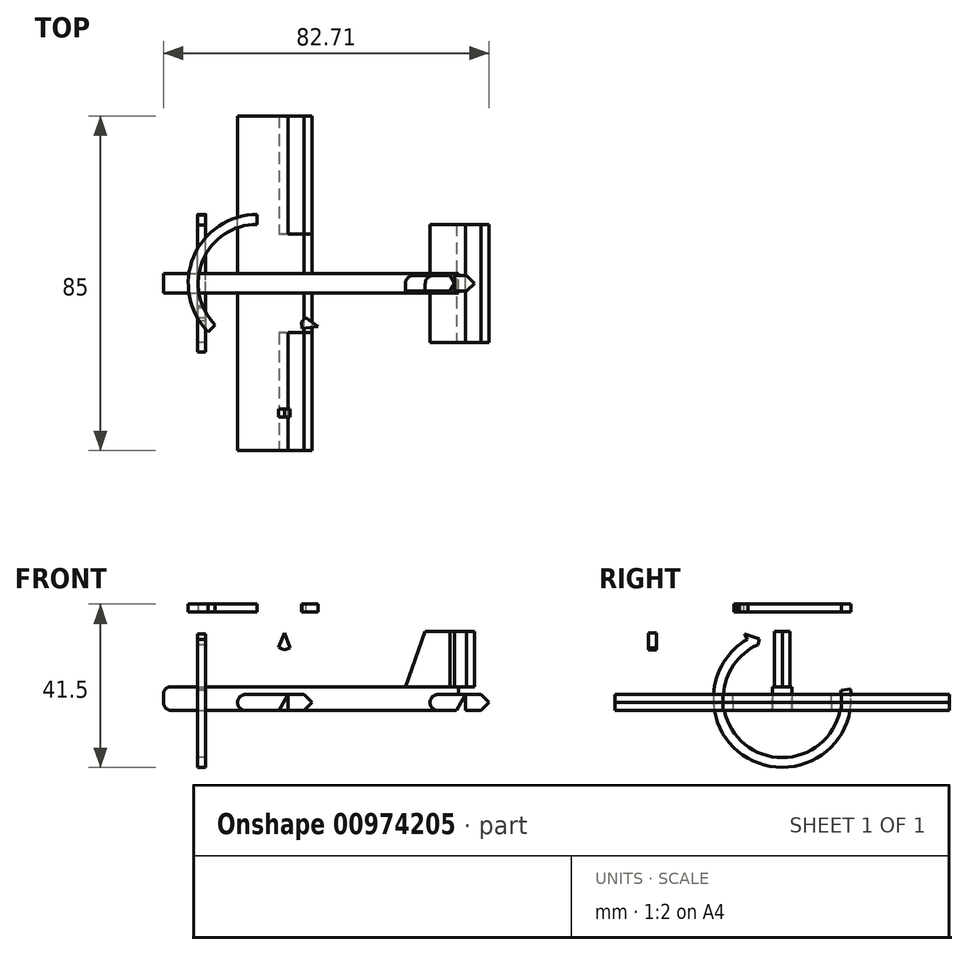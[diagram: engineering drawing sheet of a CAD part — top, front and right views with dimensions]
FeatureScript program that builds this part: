
annotation { "Feature Type Name" : "Feature", "Feature Type Description" : "" }
export const myFeature = defineFeature(function(context is Context, id is Id, definition is map)
    precondition{}
    {
        {
            var Q0;
            Q0=qCreatedBy(makeId("Top.planeOp"),FACE);
            var sketch = newSketch(context, id + "F0", { "sketchPlane" : qUnion([Q0])});
            skLineSegment(sketch, "E0.bottom", {"start": v(-58.73, 19.44) * mm, "end": v(16.27, 19.44) * mm});
            skLineSegment(sketch, "E0.top", {"start": v(-58.73, 24.44) * mm, "end": v(16.27, 24.44) * mm});
            skLineSegment(sketch, "E0.left", {"start": v(-58.73, 19.44) * mm, "end": v(-58.73, 24.44) * mm});
            skLineSegment(sketch, "E0.right", {"start": v(16.27, 19.44) * mm, "end": v(16.27, 24.44) * mm});
            skLineSegment(sketch, "E1.bottom", {"start": v(-39.92, 24.44) * mm, "end": v(-21.02, 24.44) * mm});
            skLineSegment(sketch, "E1.top", {"start": v(-39.92, 64.44) * mm, "end": v(-21.02, 64.44) * mm});
            skLineSegment(sketch, "E1.left", {"start": v(-39.92, 24.44) * mm, "end": v(-39.92, 64.44) * mm});
            skLineSegment(sketch, "E1.right", {"start": v(-21.02, 24.44) * mm, "end": v(-21.02, 64.44) * mm});
            skLineSegment(sketch, "E2.bottom", {"start": v(-39.92, 19.44) * mm, "end": v(-21.02, 19.44) * mm});
            skLineSegment(sketch, "E2.top", {"start": v(-39.92, -20.56) * mm, "end": v(-21.02, -20.56) * mm});
            skLineSegment(sketch, "E2.left", {"start": v(-39.92, 19.44) * mm, "end": v(-39.92, -20.56) * mm});
            skLineSegment(sketch, "E2.right", {"start": v(-21.02, 19.44) * mm, "end": v(-21.02, -20.56) * mm});
            skLineSegment(sketch, "E3.bottom", {"start": v(-21.02, 64.44) * mm, "end": v(-27.02, 64.44) * mm});
            skLineSegment(sketch, "E3.top", {"start": v(-21.02, 34.44) * mm, "end": v(-27.02, 34.44) * mm});
            skLineSegment(sketch, "E3.left", {"start": v(-21.02, 64.44) * mm, "end": v(-21.02, 34.44) * mm});
            skLineSegment(sketch, "E3.right", {"start": v(-27.02, 64.44) * mm, "end": v(-27.02, 34.44) * mm});
            skLineSegment(sketch, "E4.bottom", {"start": v(-21.02, -20.56) * mm, "end": v(-27.02, -20.56) * mm});
            skLineSegment(sketch, "E4.top", {"start": v(-21.02, 9.44) * mm, "end": v(-27.02, 9.44) * mm});
            skLineSegment(sketch, "E4.left", {"start": v(-21.02, -20.56) * mm, "end": v(-21.02, 9.44) * mm});
            skLineSegment(sketch, "E4.right", {"start": v(-27.02, -20.56) * mm, "end": v(-27.02, 9.44) * mm});
            skLineSegment(sketch, "E5.bottom", {"start": v(8.98, 6.94) * mm, "end": v(23.98, 6.94) * mm});
            skLineSegment(sketch, "E5.top", {"start": v(8.98, 36.94) * mm, "end": v(23.98, 36.94) * mm});
            skLineSegment(sketch, "E5.left", {"start": v(8.98, 6.94) * mm, "end": v(8.98, 19.44) * mm});
            skLineSegment(sketch, "E5.right", {"start": v(23.98, 6.94) * mm, "end": v(23.98, 36.94) * mm});
            skLineSegment(sketch, "E6.bottom", {"start": v(23.98, 6.94) * mm, "end": v(17.98, 6.94) * mm});
            skLineSegment(sketch, "E6.top", {"start": v(23.98, 36.94) * mm, "end": v(17.98, 36.94) * mm});
            skLineSegment(sketch, "E6.right", {"start": v(17.98, 6.94) * mm, "end": v(17.98, 36.94) * mm});
            skLineSegment(sketch, "E7.trimOffspring", {"start": v(8.98, 24.44) * mm, "end": v(8.98, 36.94) * mm});
            skLineSegment(sketch, "E8.bottom", {"start": v(2.77, 23.94) * mm, "end": v(15.27, 23.94) * mm});
            skLineSegment(sketch, "E8.top", {"start": v(2.77, 19.94) * mm, "end": v(15.27, 19.94) * mm});
            skLineSegment(sketch, "E8.left", {"start": v(2.77, 23.94) * mm, "end": v(2.77, 19.94) * mm});
            skLineSegment(sketch, "E8.right", {"start": v(15.27, 23.94) * mm, "end": v(15.27, 19.94) * mm});
            skSolve(sketch);
        }
        {
            var Q0;
            {var subQ1=sQuery(id+"F0.wireOp",EDGE,"E0.left");Q0=makeQuery(id+"F0.imprint","IMPRINT",FACE,{"disambiguationData":[TD([[makeQuery(id+"F0.imprint","IMPRINT",EDGE,{"derivedFrom":subQ1}),-1.0]])]});}
            var Q1;
            {var subQ1=sQuery(id+"F0.wireOp",EDGE,"E0.left");Q1=makeQuery(id+"F0.imprint","IMPRINT",FACE,{"disambiguationData":[TD([[makeQuery(id+"F0.imprint","IMPRINT",EDGE,{"derivedFrom":subQ1}),-1.0]])]});}
            extrude(context, id + "F1", {"entities" : qUnion([Q0, Q1]), "depth" : 6 * mm, "offsetDistance" : 25 * mm});
        }
        {
            var Q0;
            {var subQ4=sQuery(id+"F0.wireOp",EDGE,"E2.left");Q0=makeQuery(id+"F0.imprint","IMPRINT",FACE,{"disambiguationData":[TD([[makeQuery(id+"F0.imprint","IMPRINT",EDGE,{"derivedFrom":subQ4}),1.0]])]});}
            var Q1;
            {var subQ4=sQuery(id+"F0.wireOp",EDGE,"E1.left");Q1=makeQuery(id+"F0.imprint","IMPRINT",FACE,{"disambiguationData":[TD([[makeQuery(id+"F0.imprint","IMPRINT",EDGE,{"derivedFrom":subQ4}),-1.0]])]});}
            var Q2;
            {var subQ3=sQuery(id+"F0.wireOp",EDGE,"E0.right");Q2=makeQuery(id+"F0.imprint","IMPRINT",FACE,{"disambiguationData":[TD([[makeQuery(id+"F0.imprint","IMPRINT",EDGE,{"derivedFrom":subQ3}),-1.0]])]});}
            extrude(context, id + "F2", {"entities" : qUnion([Q0, Q1, Q2]), "operationType" : NewBodyOperationType.ADD, "depth" : 4 * mm, "offsetDistance" : 25 * mm});
        }
        {
            var Q0;
            {var subQ4=sQuery(id+"F0.wireOp",EDGE,"E4.top");Q0=makeQuery(id+"F0.imprint","IMPRINT",FACE,{"disambiguationData":[TD([[makeQuery(id+"F0.imprint","IMPRINT",EDGE,{"derivedFrom":subQ4}),1.0]])]});}
            var Q1;
            {var subQ4=sQuery(id+"F0.wireOp",EDGE,"E3.top");Q1=makeQuery(id+"F0.imprint","IMPRINT",FACE,{"disambiguationData":[TD([[makeQuery(id+"F0.imprint","IMPRINT",EDGE,{"derivedFrom":subQ4}),-1.0]])]});}
            var Q2;
            {var subQ0=sQuery(id+"F0.wireOp",EDGE,"E5.right");Q2=makeQuery(id+"F0.imprint","IMPRINT",FACE,{"disambiguationData":[TD([[makeQuery(id+"F0.imprint","IMPRINT",EDGE,{"derivedFrom":subQ0}),1.0]])]});}
            extrude(context, id + "F3", {"entities" : qUnion([Q0, Q1, Q2]), "depth" : 4 * mm, "offsetDistance" : 25 * mm});
        }
        {
            var Q0;
            Q0=makeQuery(id+"F0.imprint","IMPRINT",FACE,{"disambiguationData":[TD([[makeQuery(id+"F0.imprint","IMPRINT",EDGE,{"derivedFrom":sQuery(id+"F0.wireOp",EDGE,"E8.bottom")}),-1.0]])]});
            extrude(context, id + "F4", {"entities" : qUnion([Q0]), "operationType" : NewBodyOperationType.ADD, "depth" : 20 * mm, "offsetDistance" : 25 * mm});
        }
        {
            var Q0;
            Q0=makeQuery(id+"F4.opExtrude","SWEPT_FACE",FACE,{"disambiguationData":[OSD([sQuery(id+"F0.wireOp",EDGE,"E8.top")])]});
            cPlane(context, id + "F5", {"entities" : qUnion([Q0]), "cplaneType" : CPlaneType.OFFSET, "offset" : 0 * mm, "width" : 150 * mm, "height" : 150 * mm});
        }
        {
            var Q0;
            Q0=qCreatedBy(id+"F5.planeOp",FACE);
            var sketch = newSketch(context, id + "F6", { "sketchPlane" : qUnion([Q0])});
            skLineSegment(sketch, "E9.0.0", {"start": v(2.77, 20) * mm, "end": v(2.77, 6) * mm});
            skLineSegment(sketch, "E9.0.1", {"start": v(2.77, 6) * mm, "end": v(15.27, 6) * mm});
            skLineSegment(sketch, "E9.0.2", {"start": v(15.27, 6) * mm, "end": v(15.27, 20) * mm});
            skLineSegment(sketch, "E9.0.3", {"start": v(15.27, 20) * mm, "end": v(2.77, 20) * mm});
            skLineSegment(sketch, "E10", {"start": v(2.77, 6) * mm, "end": v(7.78, 20) * mm});
            skLineSegment(sketch, "E11", {"start": v(7.78, 20) * mm, "end": v(12.04, 20) * mm});
            skLineSegment(sketch, "E12", {"start": v(12.04, 20) * mm, "end": v(12.04, 6) * mm});
            skLineSegment(sketch, "E13", {"start": v(12.04, 6) * mm, "end": v(15.27, 6) * mm});
            skLineSegment(sketch, "E14", {"start": v(15.27, 20) * mm, "end": v(12.04, 20) * mm});
            skSolve(sketch);
        }
        {
            var Q0;
            {var subQ0=sQuery(id+"F6.wireOp",EDGE,"E9.0.0");Q0=makeQuery(id+"F6.imprint","IMPRINT",FACE,{"disambiguationData":[TD([[makeQuery(id+"F6.imprint","IMPRINT",EDGE,{"derivedFrom":subQ0}),1.0]])]});}
            extrude(context, id + "F7", {"entities" : qUnion([Q0]), "operationType" : NewBodyOperationType.REMOVE, "oppositeDirection" : true, "depth" : 25 * mm, "offsetDistance" : 25 * mm});
        }
        {
            var Q0;
            Q0=makeQuery(id+"F4.opExtrude","SWEPT_FACE",FACE,{"disambiguationData":[OSD([sQuery(id+"F0.wireOp",EDGE,"E8.right")])]});
            extrude(context, id + "F8", {"entities" : qUnion([Q0]), "depth" : 5 * mm, "offsetDistance" : 25 * mm});
        }
        {
            var Q0;
            Q0=makeQuery(id+"F2.opExtrude","CAP_EDGE",EDGE,{"disambiguationData":[OSD([sQuery(id+"F0.wireOp",EDGE,"E2.left")])],"isStart":false});
            var Q1;
            Q1=makeQuery(id+"F2.opExtrude","CAP_EDGE",EDGE,{"disambiguationData":[OSD([sQuery(id+"F0.wireOp",EDGE,"E1.left")])],"isStart":false});
            var Q2;
            Q2=makeQuery(id+"F2.opExtrude","CAP_EDGE",EDGE,{"disambiguationData":[OSD([sQuery(id+"F0.wireOp",EDGE,"E5.left")])],"isStart":false});
            var Q3;
            Q3=makeQuery(id+"F2.opExtrude","CAP_EDGE",EDGE,{"disambiguationData":[OSD([sQuery(id+"F0.wireOp",EDGE,"E5.left")])],"isStart":false});
            var Q4;
            Q4=makeQuery(id+"F2.opExtrude","CAP_EDGE",EDGE,{"disambiguationData":[OSD([sQuery(id+"F0.wireOp",EDGE,"E2.left")])],"isStart":true});
            var Q5;
            Q5=makeQuery(id+"F2.opExtrude","CAP_EDGE",EDGE,{"disambiguationData":[OSD([sQuery(id+"F0.wireOp",EDGE,"E1.left")])],"isStart":true});
            var Q6;
            Q6=makeQuery(id+"F2.opExtrude","CAP_EDGE",EDGE,{"disambiguationData":[OSD([sQuery(id+"F0.wireOp",EDGE,"E5.left")])],"isStart":true});
            var Q7;
            Q7=makeQuery(id+"F2.opExtrude","CAP_EDGE",EDGE,{"disambiguationData":[OSD([sQuery(id+"F0.wireOp",EDGE,"E5.left")])],"isStart":true});
            var Q8;
            Q8=makeQuery(id+"F1.opExtrude","CAP_EDGE",EDGE,{"disambiguationData":[OSD([sQuery(id+"F0.wireOp",EDGE,"E0.left")])],"isStart":false});
            var Q9;
            Q9=makeQuery(id+"F1.opExtrude","CAP_EDGE",EDGE,{"disambiguationData":[OSD([sQuery(id+"F0.wireOp",EDGE,"E0.left")])],"isStart":true});
            var Q10;
            Q10=makeQuery(id+"F2.opExtrude","CAP_EDGE",EDGE,{"disambiguationData":[OSD([sQuery(id+"F0.wireOp",EDGE,"E7.trimOffspring")])],"isStart":false});
            var Q11;
            Q11=makeQuery(id+"F2.opExtrude","CAP_EDGE",EDGE,{"disambiguationData":[OSD([sQuery(id+"F0.wireOp",EDGE,"E7.trimOffspring")])],"isStart":true});
            var Q12;
            Q12=makeQuery(id+"F7.boolean.opBoolean","COPY",EDGE,{"derivedFrom":makeQuery(id+"F7.opExtrude","CAP_EDGE",EDGE,{"disambiguationData":[OSD([sQuery(id+"F6.wireOp",EDGE,"E10")])],"isStart":true})});
            var Q13;
            Q13=makeQuery(id+"F7.boolean.opBoolean","INTERSECT",EDGE,{"derivedFrom":[makeQuery(id+"F4.opExtrude","SWEPT_FACE",FACE,{"disambiguationData":[OSD([sQuery(id+"F0.wireOp",EDGE,"E8.bottom")])]}),makeQuery(id+"F7.opExtrude","SWEPT_FACE",FACE,{"disambiguationData":[OSD([sQuery(id+"F6.wireOp",EDGE,"E10")])]})]});
            fillet(context, id + "F9", {"entities" : qUnion([Q0, Q1, Q2, Q3, Q4, Q5, Q6, Q7, Q8, Q9, Q10, Q11, Q12, Q13]), "radius" : 2 * mm, "tangentPropagation" : true, "allowEdgeOverflow" : false});
        }
        {
            var Q0;
            Q0=makeQuery(id+"F3.opExtrude","CAP_EDGE",EDGE,{"disambiguationData":[OSD([sQuery(id+"F0.wireOp",EDGE,"E2.right")])],"isStart":false});
            var Q1;
            Q1=makeQuery(id+"F2.opExtrude","CAP_EDGE",EDGE,{"disambiguationData":[OSD([sQuery(id+"F0.wireOp",EDGE,"E2.right")])],"isStart":false});
            var Q2;
            Q2=makeQuery(id+"F3.opExtrude","CAP_EDGE",EDGE,{"disambiguationData":[OSD([sQuery(id+"F0.wireOp",EDGE,"E1.right")])],"isStart":false});
            var Q3;
            Q3=makeQuery(id+"F2.opExtrude","CAP_EDGE",EDGE,{"disambiguationData":[OSD([sQuery(id+"F0.wireOp",EDGE,"E1.right")])],"isStart":false});
            var Q4;
            Q4=makeQuery(id+"F3.opExtrude","CAP_EDGE",EDGE,{"disambiguationData":[OSD([sQuery(id+"F0.wireOp",EDGE,"E5.right")])],"isStart":false});
            var Q5;
            Q5=makeQuery(id+"F3.opExtrude","CAP_EDGE",EDGE,{"disambiguationData":[OSD([sQuery(id+"F0.wireOp",EDGE,"E2.right")])],"isStart":true});
            var Q6;
            Q6=makeQuery(id+"F2.opExtrude","CAP_EDGE",EDGE,{"disambiguationData":[OSD([sQuery(id+"F0.wireOp",EDGE,"E2.right")])],"isStart":true});
            var Q7;
            Q7=makeQuery(id+"F2.opExtrude","CAP_EDGE",EDGE,{"disambiguationData":[OSD([sQuery(id+"F0.wireOp",EDGE,"E1.right")])],"isStart":true});
            var Q8;
            Q8=makeQuery(id+"F3.opExtrude","CAP_EDGE",EDGE,{"disambiguationData":[OSD([sQuery(id+"F0.wireOp",EDGE,"E1.right")])],"isStart":true});
            var Q9;
            Q9=makeQuery(id+"F3.opExtrude","CAP_EDGE",EDGE,{"disambiguationData":[OSD([sQuery(id+"F0.wireOp",EDGE,"E5.right")])],"isStart":true});
            var Q10;
            Q10=makeQuery(id+"F8.opExtrude","CAP_EDGE",EDGE,{"disambiguationData":[OSD([sQuery(id+"F0.wireOp",EDGE,"E8.top"),sQuery(id+"F0.wireOp",EDGE,"E8.right")])],"isStart":false});
            var Q11;
            Q11=makeQuery(id+"F8.opExtrude","CAP_EDGE",EDGE,{"disambiguationData":[OSD([sQuery(id+"F0.wireOp",EDGE,"E8.bottom"),sQuery(id+"F0.wireOp",EDGE,"E8.right")])],"isStart":false});
            chamfer(context, id + "F10", {"entities" : qUnion([Q0, Q1, Q2, Q3, Q4, Q5, Q6, Q7, Q8, Q9, Q10, Q11]), "width" : 2 * mm, "tangentPropagation" : true});
        }
        {
            var Q0;
            Q0=makeQuery(id+"F2.opExtrude","CAP_EDGE",EDGE,{"disambiguationData":[OSD([sQuery(id+"F0.wireOp",EDGE,"E4.right")])],"isStart":true});
            var Q1;
            Q1=makeQuery(id+"F2.opExtrude","CAP_EDGE",EDGE,{"disambiguationData":[OSD([sQuery(id+"F0.wireOp",EDGE,"E3.right")])],"isStart":true});
            var Q2;
            Q2=makeQuery(id+"F2.opExtrude","CAP_EDGE",EDGE,{"disambiguationData":[OSD([sQuery(id+"F0.wireOp",EDGE,"E6.right")])],"isStart":true});
            chamfer(context, id + "F11", {"entities" : qUnion([Q0, Q1, Q2]), "chamferType" : ChamferType.OFFSET_ANGLE, "width" : 4 * mm, "oppositeDirection" : false, "angle" : 30 * degree, "tangentPropagation" : true});
        }
        {
            var Q0;
            Q0=makeQuery(id+"F4.opExtrude","SWEPT_EDGE",EDGE,{"disambiguationData":[OSD([sQuery(id+"F0.wireOp",EDGE,"E8.top"),sQuery(id+"F0.wireOp",EDGE,"E8.right")])]});
            var Q1;
            Q1=makeQuery(id+"F4.opExtrude","SWEPT_EDGE",EDGE,{"disambiguationData":[OSD([sQuery(id+"F0.wireOp",EDGE,"E8.bottom"),sQuery(id+"F0.wireOp",EDGE,"E8.right")])]});
            chamfer(context, id + "F12", {"entities" : qUnion([Q0, Q1]), "chamferType" : ChamferType.OFFSET_ANGLE, "width" : 2 * mm, "oppositeDirection" : false, "angle" : 30 * degree, "tangentPropagation" : true});
        }
        {
            var Q0;
            Q0=qCreatedBy(makeId("Right.planeOp"),FACE);
            cPlane(context, id + "F13", {"entities" : qUnion([Q0]), "cplaneType" : CPlaneType.OFFSET, "offset" : 50 * mm, "oppositeDirection" : true, "width" : 150 * mm, "height" : 150 * mm});
        }
        {
            var Q0;
            Q0=qCreatedBy(id+"F13.planeOp",FACE);
            var sketch = newSketch(context, id + "F14", { "sketchPlane" : qUnion([Q0])});
            skLineSegment(sketch, "E15.0.0", {"start": v(24.44, 4) * mm, "end": v(24.44, 2) * mm});
            skLineSegment(sketch, "E15.0.1", {"start": v(24.44, 2) * mm, "end": v(19.44, 2) * mm});
            skLineSegment(sketch, "E15.0.2", {"start": v(19.44, 2) * mm, "end": v(19.44, 4) * mm});
            skLineSegment(sketch, "E15.0.3", {"start": v(19.44, 4) * mm, "end": v(24.44, 4) * mm});
            skLineSegment(sketch, "E16", {"start": v(24.44, 2) * mm, "end": v(19.44, 4) * mm});
            skLineSegment(sketch, "E17", {"start": v(19.44, 2) * mm, "end": v(24.44, 4) * mm});
            skCircle(sketch, "E18", {"center": v(21.94, 3) * mm, "radius": 15 * mm});
            skCircle(sketch, "E19", {"center": v(21.94, 3) * mm, "radius": 17.5 * mm});
            skLineSegment(sketch, "E20", {"start": v(21.94, 3) * mm, "end": v(30.51, -12.26) * mm});
            skLineSegment(sketch, "E21", {"start": v(21.94, 3) * mm, "end": v(13.07, 18.09) * mm});
            skLineSegment(sketch, "E22", {"start": v(21.94, 3) * mm, "end": v(15.77, 19.38) * mm});
            skLineSegment(sketch, "E23", {"start": v(15.77, 19.38) * mm, "end": v(16.21, 18.2) * mm});
            skLineSegment(sketch, "E24", {"start": v(13.07, 18.09) * mm, "end": v(12.3, 19.38) * mm});
            skLineSegment(sketch, "E25", {"start": v(14.33, 15.93) * mm, "end": v(15.1, 14.64) * mm});
            skLineSegment(sketch, "E26", {"start": v(12.3, 19.38) * mm, "end": v(16.21, 18.2) * mm});
            skLineSegment(sketch, "E27", {"start": v(15.1, 14.64) * mm, "end": v(16.21, 18.2) * mm});
            skLineSegment(sketch, "E28", {"start": v(21.94, 3) * mm, "end": v(39.26, 5.48) * mm});
            skSolve(sketch);
        }
        {
            var Q0;
            {var subQ3=sQuery(id+"F14.wireOp",EDGE,"E20");var subQ5=sQuery(id+"F14.wireOp",EDGE,"E19");var subQ6=makeQuery(id+"F14.imprint","INTERSECT",VERTEX,{"derivedFrom":[subQ5,subQ3]});Q0=makeQuery(id+"F14.imprint","IMPRINT",FACE,{"disambiguationData":[TD([[makeQuery(id+"F14.imprint","IMPRINT",EDGE,{"disambiguationData":[TD([[subQ6,1.0]])],"derivedFrom":subQ3}),-1.0]])]});}
            var Q1;
            {var subQ3=sQuery(id+"F14.wireOp",EDGE,"E18");var subQ7=sQuery(id+"F14.wireOp",EDGE,"E27");var subQ9=makeQuery(id+"F14.imprint","INTERSECT",VERTEX,{"derivedFrom":[subQ3,subQ7]});Q1=makeQuery(id+"F14.imprint","IMPRINT",FACE,{"disambiguationData":[TD([[makeQuery(id+"F14.imprint","IMPRINT",EDGE,{"disambiguationData":[TD([[subQ9,-1.0]])],"derivedFrom":subQ3}),-1.0]])]});}
            var Q2;
            {var subQ0=sQuery(id+"F14.wireOp",EDGE,"E25");Q2=makeQuery(id+"F14.imprint","IMPRINT",FACE,{"disambiguationData":[TD([[makeQuery(id+"F14.imprint","IMPRINT",EDGE,{"derivedFrom":subQ0}),1.0]])]});}
            var Q3;
            {var subQ0=sQuery(id+"F14.wireOp",EDGE,"E24");Q3=makeQuery(id+"F14.imprint","IMPRINT",FACE,{"disambiguationData":[TD([[makeQuery(id+"F14.imprint","IMPRINT",EDGE,{"derivedFrom":subQ0}),-1.0]])]});}
            var Q4;
            {var subQ0=sQuery(id+"F14.wireOp",EDGE,"E28");var subQ1=sQuery(id+"F14.wireOp",EDGE,"E18");var subQ2=makeQuery(id+"F14.imprint","INTERSECT",VERTEX,{"derivedFrom":[subQ1,subQ0]});Q4=makeQuery(id+"F14.imprint","IMPRINT",FACE,{"disambiguationData":[TD([[makeQuery(id+"F14.imprint","IMPRINT",EDGE,{"disambiguationData":[TD([[subQ2,1.0]])],"derivedFrom":subQ1}),-1.0]])]});}
            extrude(context, id + "F15", {"entities" : qUnion([Q0, Q1, Q2, Q3, Q4]), "depth" : 2 * mm, "offsetDistance" : 25 * mm});
        }
        {
            var Q0;
            Q0=qCreatedBy(makeId("Front.planeOp"),FACE);
            cPlane(context, id + "F16", {"entities" : qUnion([Q0]), "cplaneType" : CPlaneType.OFFSET, "offset" : 10 * mm, "width" : 150 * mm, "height" : 150 * mm});
        }
        {
            var Q0;
            Q0=qCreatedBy(id+"F16.planeOp",FACE);
            var sketch = newSketch(context, id + "F17", { "sketchPlane" : qUnion([Q0])});
            skLineSegment(sketch, "E29.0.0", {"start": v(-37.92, 0) * mm, "end": v(-29.33, 0) * mm});
            skLineSegment(sketch, "E29.0.1", {"start": v(-29.33, 0) * mm, "end": v(-27.02, 4) * mm});
            skLineSegment(sketch, "E29.0.2", {"start": v(-27.02, 4) * mm, "end": v(-37.92, 4) * mm});
            skArc(sketch, "E29.0.3", {"start": v(-37.92, 4) * mm, "mid": v(-39.92, 2) * mm, "end": v(-37.92, 0) * mm});
            skLineSegment(sketch, "E30", {"start": v(-37.92, 2) * mm, "end": v(-34.92, 2) * mm});
            skCircle(sketch, "E31", {"center": v(-34.92, 2) * mm, "radius": 17.5 * mm});
            skCircle(sketch, "E32", {"center": v(-34.92, 2) * mm, "radius": 15 * mm});
            skLineSegment(sketch, "E33", {"start": v(-34.92, 2) * mm, "end": v(-22.42, -10.25) * mm});
            skLineSegment(sketch, "E34", {"start": v(-22.42, -10.25) * mm, "end": v(-34.92, 2) * mm});
            skLineSegment(sketch, "E35", {"start": v(-34.92, 2) * mm, "end": v(-28.57, 18.3) * mm});
            skLineSegment(sketch, "E36", {"start": v(-28.57, 18.3) * mm, "end": v(-28.02, 19.7) * mm});
            skLineSegment(sketch, "E37", {"start": v(-29.47, 15.98) * mm, "end": v(-30.02, 14.58) * mm});
            skLineSegment(sketch, "E38", {"start": v(-34.92, 2) * mm, "end": v(-25.88, 16.98) * mm});
            skLineSegment(sketch, "E39", {"start": v(-25.88, 16.98) * mm, "end": v(-26.52, 15.91) * mm});
            skLineSegment(sketch, "E40", {"start": v(-28.02, 19.7) * mm, "end": v(-26.52, 15.91) * mm});
            skLineSegment(sketch, "E41", {"start": v(-30.02, 14.58) * mm, "end": v(-26.52, 15.91) * mm});
            skSolve(sketch);
        }
        {
            var Q0;
            {var subQ0=sQuery(id+"F17.wireOp",EDGE,"E34");var subQ1=sQuery(id+"F17.wireOp",EDGE,"E31");var subQ2=makeQuery(id+"F17.imprint","INTERSECT",VERTEX,{"derivedFrom":[subQ1,subQ0]});Q0=makeQuery(id+"F17.imprint","IMPRINT",FACE,{"disambiguationData":[TD([[makeQuery(id+"F17.imprint","IMPRINT",EDGE,{"disambiguationData":[TD([[subQ2,-1.0]])],"derivedFrom":subQ0}),1.0]])]});}
            var Q1;
            {var subQ0=sQuery(id+"F17.wireOp",EDGE,"E37");Q1=makeQuery(id+"F17.imprint","IMPRINT",FACE,{"disambiguationData":[TD([[makeQuery(id+"F17.imprint","IMPRINT",EDGE,{"derivedFrom":subQ0}),1.0]])]});}
            var Q2;
            {var subQ1=sQuery(id+"F17.wireOp",EDGE,"E31");var subQ7=sQuery(id+"F17.wireOp",EDGE,"E40");var subQ9=makeQuery(id+"F17.imprint","INTERSECT",VERTEX,{"derivedFrom":[subQ1,subQ7]});Q2=makeQuery(id+"F17.imprint","IMPRINT",FACE,{"disambiguationData":[TD([[makeQuery(id+"F17.imprint","IMPRINT",EDGE,{"disambiguationData":[TD([[subQ9,-1.0]])],"derivedFrom":subQ1}),1.0]])]});}
            var Q3;
            {var subQ0=sQuery(id+"F17.wireOp",EDGE,"E36");Q3=makeQuery(id+"F17.imprint","IMPRINT",FACE,{"disambiguationData":[TD([[makeQuery(id+"F17.imprint","IMPRINT",EDGE,{"derivedFrom":subQ0}),-1.0]])]});}
            extrude(context, id + "F18", {"entities" : qUnion([Q0, Q1, Q2, Q3]), "depth" : 2 * mm, "offsetDistance" : 25 * mm});
        }
        {
            var Q0;
            Q0=qCreatedBy(makeId("Top.planeOp"),FACE);
            cPlane(context, id + "F19", {"entities" : qUnion([Q0]), "cplaneType" : CPlaneType.OFFSET, "offset" : 25 * mm, "width" : 150 * mm, "height" : 150 * mm});
        }
        {
            var Q0;
            Q0=qCreatedBy(id+"F19.planeOp",FACE);
            var sketch = newSketch(context, id + "F20", { "sketchPlane" : qUnion([Q0])});
            skPoint(sketch, "E42.0", {"position": v(-34.92, -10) * mm});
            skPoint(sketch, "E43.0", {"position": v(-50, 21.94) * mm});
            skLineSegment(sketch, "E44", {"start": v(-34.92, -10) * mm, "end": v(-34.92, 46.54) * mm});
            skLineSegment(sketch, "E45", {"start": v(-50, 21.94) * mm, "end": v(-34.92, 21.94) * mm});
            skCircle(sketch, "E46", {"center": v(-34.92, 21.94) * mm, "radius": 17.5 * mm});
            skCircle(sketch, "E47", {"center": v(-34.92, 21.94) * mm, "radius": 15 * mm});
            skLineSegment(sketch, "E48", {"start": v(-34.92, 21.94) * mm, "end": v(-50.72, 29.45) * mm});
            skLineSegment(sketch, "E49", {"start": v(-34.92, 21.94) * mm, "end": v(-20.65, 11.8) * mm});
            skLineSegment(sketch, "E50", {"start": v(-34.92, 21.94) * mm, "end": v(-22.59, 9.52) * mm});
            skLineSegment(sketch, "E51", {"start": v(-22.69, 13.25) * mm, "end": v(-23.9, 14.12) * mm});
            skLineSegment(sketch, "E52", {"start": v(-20.65, 11.8) * mm, "end": v(-19.42, 10.94) * mm});
            skLineSegment(sketch, "E53", {"start": v(-22.59, 9.52) * mm, "end": v(-23.47, 10.4) * mm});
            skLineSegment(sketch, "E54", {"start": v(-23.47, 10.4) * mm, "end": v(-23.9, 14.12) * mm});
            skLineSegment(sketch, "E55", {"start": v(-23.47, 10.4) * mm, "end": v(-19.42, 10.94) * mm});
            skLineSegment(sketch, "E56", {"start": v(-34.92, 21.94) * mm, "end": v(-47.34, 9.6) * mm});
            skSolve(sketch);
        }
        {
            var Q0;
            {var subQ0=sQuery(id+"F20.wireOp",EDGE,"E48");var subQ1=sQuery(id+"F20.wireOp",EDGE,"E46");var subQ2=makeQuery(id+"F20.imprint","INTERSECT",VERTEX,{"derivedFrom":[subQ1,subQ0]});Q0=makeQuery(id+"F20.imprint","IMPRINT",FACE,{"disambiguationData":[TD([[makeQuery(id+"F20.imprint","IMPRINT",EDGE,{"disambiguationData":[TD([[subQ2,1.0]])],"derivedFrom":subQ0}),-1.0]])]});}
            var Q1;
            {var subQ0=sQuery(id+"F20.wireOp",EDGE,"E51");Q1=makeQuery(id+"F20.imprint","IMPRINT",FACE,{"disambiguationData":[TD([[makeQuery(id+"F20.imprint","IMPRINT",EDGE,{"derivedFrom":subQ0}),1.0]])]});}
            var Q2;
            {var subQ0=sQuery(id+"F20.wireOp",EDGE,"E55");var subQ7=sQuery(id+"F20.wireOp",EDGE,"E46");var subQ9=makeQuery(id+"F20.imprint","INTERSECT",VERTEX,{"derivedFrom":[subQ7,subQ0]});Q2=makeQuery(id+"F20.imprint","IMPRINT",FACE,{"disambiguationData":[TD([[makeQuery(id+"F20.imprint","IMPRINT",EDGE,{"disambiguationData":[TD([[subQ9,-1.0]])],"derivedFrom":subQ7}),1.0]])]});}
            var Q3;
            {var subQ0=sQuery(id+"F20.wireOp",EDGE,"E52");Q3=makeQuery(id+"F20.imprint","IMPRINT",FACE,{"disambiguationData":[TD([[makeQuery(id+"F20.imprint","IMPRINT",EDGE,{"derivedFrom":subQ0}),-1.0]])]});}
            var Q4;
            {var subQ0=sQuery(id+"F20.wireOp",EDGE,"E48");var subQ1=sQuery(id+"F20.wireOp",EDGE,"E46");var subQ2=makeQuery(id+"F20.imprint","INTERSECT",VERTEX,{"derivedFrom":[subQ1,subQ0]});Q4=makeQuery(id+"F20.imprint","IMPRINT",FACE,{"disambiguationData":[TD([[makeQuery(id+"F20.imprint","IMPRINT",EDGE,{"disambiguationData":[TD([[subQ2,-1.0]])],"derivedFrom":subQ1}),1.0]])]});}
            var Q5;
            {var subQ0=sQuery(id+"F20.wireOp",EDGE,"E46");var subQ1=sQuery(id+"F20.wireOp",EDGE,"E44");var subQ2=makeQuery(id+"F20.imprint","INTERSECT",VERTEX,{"disambiguationData":[OD(1.0)],"derivedFrom":[subQ1,subQ0]});Q5=makeQuery(id+"F20.imprint","IMPRINT",FACE,{"disambiguationData":[TD([[makeQuery(id+"F20.imprint","IMPRINT",EDGE,{"disambiguationData":[TD([[subQ2,1.0]])],"derivedFrom":subQ1}),-1.0]])]});}
            extrude(context, id + "F21", {"entities" : qUnion([Q0, Q1, Q2, Q3, Q4, Q5]), "depth" : 2 * mm, "offsetDistance" : 25 * mm});
        }
    });
